# Revit family: DVS-G
name_source: partatom
category: Wyposażenie mechaniczne
revit_build: Autodesk Revit 2017 (Build: 20160225_1515(x64)
units: mm (PartAtom-declared; Revit-internal decimal feet)

## family parameters
Oparty na płaszczyźnie roboczej = Nie
Punkt obliczania pomieszczeń = Nie
Tnij formami wycięć po wczytaniu = Nie
Typ części = Normalny
Współdzielony = Nie
Wymiar okrągłego złącza = Użyj średnicy
Zawsze pionowo = Tak

## types (16) — shared parameters
Date = 09.2018
Frequency = 50 Hz
Producent = Rosenberg
Text_1 = 340 mm
Text_2 = 170 mm
URL = https://www.rosenberg.pl
Version = 1

## per-type parameters (varying)
| type | A | Air_flow | Current | Da | Di | H | Height | L | Model | P | Power | Pressure | Protection_class | Text_size | Voltage | Weight[kg] | Width | Width_bottom | max.Ambient_temperature | t1 |
| 190-G.3BK | 294 mm  [stored 0.964567 ft] | 374.0 m³/h | 1 A | 235 mm  [stored 0.770997 ft] | 186 mm  [stored 0.610236 ft] | 600 mm | 290 mm  [stored 0.951444 ft] | 115 mm  [stored 0.377297 ft] | 190-G.3BK | 571 mm  [stored 1.87336 ft] | 0 kW | 455.0 Pa | IP44 | 15 mm  [stored 0.0492126 ft] | 230 V | 9.8 | 540 mm  [stored 1.77165 ft] | 335 mm  [stored 1.09908 ft] | 50 °C | 2 mm  [stored 0.00656168 ft] |
| 225-G.3BK | 294 mm  [stored 0.964567 ft] | 374.0 m³/h | 1 A | 235 mm  [stored 0.770997 ft] | 186 mm  [stored 0.610236 ft] | 600 mm | 290 mm  [stored 0.951444 ft] | 115 mm  [stored 0.377297 ft] | 225-G.3BK | 571 mm  [stored 1.87336 ft] | 0 kW | 455.0 Pa | IP44 | 20 mm  [stored 0.0656168 ft] | 230 V | 10.3 | 540 mm  [stored 1.77165 ft] | 335 mm  [stored 1.09908 ft] | 50 °C | 2 mm  [stored 0.00656168 ft] |
| 250-G.3DI | 395 mm  [stored 1.29593 ft] | 886.0 m³/h | 1 A | 306 mm  [stored 1.00394 ft] | 256 mm  [stored 0.839895 ft] | 700 mm | 390 mm  [stored 1.27953 ft] | 156 mm  [stored 0.511811 ft] | 250-G.3DI | 657 mm | 0 kW | 626.0 Pa | IP54 | 25 mm  [stored 0.082021 ft] | 230 V | 18.5 | 720 mm | 435 mm  [stored 1.42717 ft] | 50 °C | 2 mm  [stored 0.00656168 ft] |
| 310-G.3DI | 395 mm  [stored 1.29593 ft] | 1422.0 m³/h | 1 A | 306 mm  [stored 1.00394 ft] | 256 mm  [stored 0.839895 ft] | 700 mm | 390 mm  [stored 1.27953 ft] | 156 mm  [stored 0.511811 ft] | 310-G.3DI
310-G.3DI | 657 mm | 0 kW | 339.0 Pa | IP54 | 25 mm  [stored 0.082021 ft] | 230 V | 20 | 720 mm | 435 mm  [stored 1.42717 ft] | 50 °C | 2 mm  [stored 0.00656168 ft] |
| 355-G.4EA | 555 mm  [stored 1.82087 ft] | 2152.0 m³/h | 3 A | 464 mm  [stored 1.52231 ft] | 402 mm  [stored 1.3189 ft] | 900 mm | 445 mm  [stored 1.45997 ft] | 220 mm  [stored 0.721785 ft] | 355-G.4EA | 817 mm | 0 kW | 353.0 Pa | IP54 | 30 mm  [stored 0.0984252 ft] | 230 V | 34 | 915 mm | 595 mm  [stored 1.9521 ft] | 50 °C | 2 mm  [stored 0.00656168 ft] |
| 400-G.4FF | 555 mm  [stored 1.82087 ft] | 2349.0 m³/h | 3 A | 464 mm  [stored 1.52231 ft] | 402 mm  [stored 1.3189 ft] | 900 mm | 445 mm  [stored 1.45997 ft] | 220 mm  [stored 0.721785 ft] | 400-G.4FF | 817 mm | 0 kW | 328.0 Pa | IP54 | 35 mm  [stored 0.114829 ft] | 230 V | 34.5 | 915 mm | 595 mm  [stored 1.9521 ft] | 45 °C | 2 mm  [stored 0.00656168 ft] |
| 400-G.5FA | 555 mm  [stored 1.82087 ft] | 2766.0 m³/h | 4 A | 464 mm  [stored 1.52231 ft] | 402 mm  [stored 1.3189 ft] | 900 mm | 445 mm  [stored 1.45997 ft] | 220 mm  [stored 0.721785 ft] | 400-G.5FA | 817 mm | 1 kW | 563.0 Pa | IP54 | 35 mm  [stored 0.114829 ft] | 230 V | 34.5 | 915 mm | 595 mm  [stored 1.9521 ft] | 50 °C | 2 mm  [stored 0.00656168 ft] |
| 450-G.5FA | 625 mm  [stored 2.05052 ft] | 4245.0 m³/h | 5 A | 464 mm  [stored 1.52231 ft] | 402 mm  [stored 1.3189 ft] | 900 mm | 480 mm  [stored 1.5748 ft] | 220 mm  [stored 0.721785 ft] | 450-G.5FA | 877 mm | 1 kW | 491.0 Pa | IP54 | 40 mm  [stored 0.131234 ft] | 230 V | 47 | 1005 mm | 665 mm | 45 °C | 2 mm  [stored 0.00656168 ft] |
| 500-G.5HF | 625 mm  [stored 2.05052 ft] | 4404.0 m³/h | 5 A | 464 mm  [stored 1.52231 ft] | 402 mm  [stored 1.3189 ft] | 900 mm | 480 mm  [stored 1.5748 ft] | 220 mm  [stored 0.721785 ft] | 500-G.5HF | 877 mm | 1 kW | 456.0 Pa | IP54 | 50 mm  [stored 0.164042 ft] | 230 V | 64 | 1005 mm | 665 mm | 45 °C | 2 mm  [stored 0.00656168 ft] |
| 355-G.5FA | 555 mm  [stored 1.82087 ft] | 2094.0 m³/h | 1 A | 464 mm  [stored 1.52231 ft] | 402 mm  [stored 1.3189 ft] | 900 mm | 445 mm  [stored 1.45997 ft] | 220 mm  [stored 0.721785 ft] | 355-G.5FA | 817 mm | 1 kW | 418.0 Pa | IP54 | 30 mm  [stored 0.0984252 ft] | 400 V | 39 | 915 mm | 595 mm  [stored 1.9521 ft] | 60 °C | 2 mm  [stored 0.00656168 ft] |
| 400-G.5HF | 555 mm  [stored 1.82087 ft] | 2721.0 m³/h | 2 A | 464 mm  [stored 1.52231 ft] | 402 mm  [stored 1.3189 ft] | 900 mm | 445 mm  [stored 1.45997 ft] | 220 mm  [stored 0.721785 ft] | 400-G.5HF | 817 mm | 1 kW | 544.0 Pa | IP54 | 35 mm  [stored 0.114829 ft] | 400 V | 40 | 915 mm | 595 mm  [stored 1.9521 ft] | 55 °C | 2 mm  [stored 0.00656168 ft] |
| 450-G.5HF | 625 mm  [stored 2.05052 ft] | 4624.0 m³/h | 3 A | 464 mm  [stored 1.52231 ft] | 402 mm  [stored 1.3189 ft] | 900 mm | 480 mm  [stored 1.5748 ft] | 220 mm  [stored 0.721785 ft] | 450-G.5HF | 877 mm | 2 kW | 655.0 Pa | IP54 | 40 mm  [stored 0.131234 ft] | 400 V | 47 | 1005 mm | 665 mm | 55 °C | 2 mm  [stored 0.00656168 ft] |
| 500-G.6FF | 625 mm  [stored 2.05052 ft] | 5821.0 m³/h | 3 A | 464 mm  [stored 1.52231 ft] | 402 mm  [stored 1.3189 ft] | 900 mm | 480 mm  [stored 1.5748 ft] | 220 mm  [stored 0.721785 ft] | 500-G.5HF | 877 mm | 3 kW | 876.0 Pa | IP54 | 15 mm  [stored 0.0492126 ft] | 400 V | 48.5 | 1005 mm | 665 mm | 60 °C | 2 mm  [stored 0.00656168 ft] |
| 560-G.6IF | 895 mm | 7928.0 m³/h | 5 A | 639 mm  [stored 2.09646 ft] | 569 mm  [stored 1.8668 ft] | 1070 mm | 600 mm | 255 mm  [stored 0.836614 ft] | 560-G.6IF | 1200 mm | 3 kW | 781.0 Pa | IP54 | 50 mm  [stored 0.164042 ft] | 400 V | 88 | 1405 mm | 939 mm | 50 °C | 2 mm  [stored 0.00656168 ft] |
| 630-G.6IF | 895 mm | 7010.0 m³/h | 3 A | 639 mm  [stored 2.09646 ft] | 569 mm  [stored 1.8668 ft] | 1070 mm | 600 mm | 255 mm  [stored 0.836614 ft] | 630-G.6IF | 1200 mm | 2 kW | 434.0 Pa | IP54 | 50 mm  [stored 0.164042 ft] | 400 V | 91 | 1405 mm | 939 mm | 50 °C | 2 mm  [stored 0.00656168 ft] |
| 710-G.6NA | 985 mm | 9820.0 m³/h | 4 A | 708 mm | 635 mm | 1160 mm | 700 mm | 250 mm  [stored 0.82021 ft] | 710-G.6NA | 1300 mm | 3 kW | 517.0 Pa | IP54 | 50 mm  [stored 0.164042 ft] | 400 V | 130 | 1510 mm | 1035 mm | 50 °C | 4 mm  [stored 0.0131234 ft] |

note: [stored X ft] marks values corroborated as IEEE doubles in the binary element streams (Revit-internal decimal feet)
